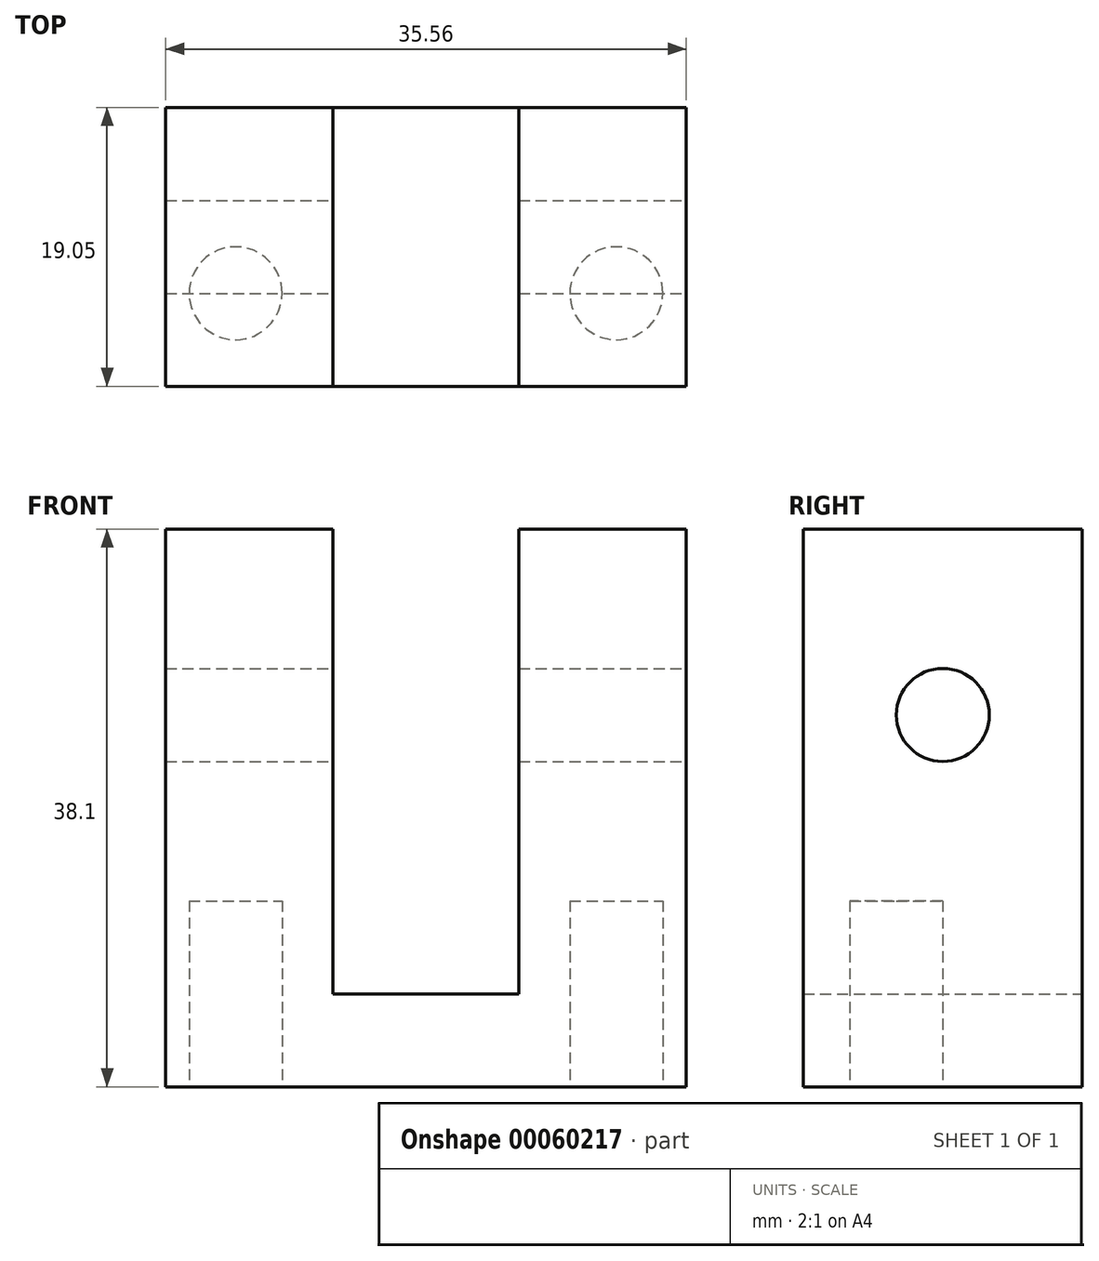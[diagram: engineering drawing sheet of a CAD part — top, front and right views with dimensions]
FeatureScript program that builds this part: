
annotation { "Feature Type Name" : "Feature", "Feature Type Description" : "" }
export const myFeature = defineFeature(function(context is Context, id is Id, definition is map)
    precondition{}
    {
        {
            var Q0;
            Q0=qCreatedBy(makeId("Front.planeOp"),FACE);
            var sketch = newSketch(context, id + "F0", { "sketchPlane" : qUnion([Q0])});
            skLineSegment(sketch, "E0", {"start": v(-17.78, 0) * mm, "end": v(-17.78, 38.1) * mm});
            skLineSegment(sketch, "E1", {"start": v(-17.78, 38.1) * mm, "end": v(-6.35, 38.1) * mm});
            skLineSegment(sketch, "E2", {"start": v(-6.35, 38.1) * mm, "end": v(-6.35, 6.35) * mm});
            skLineSegment(sketch, "E3", {"start": v(-6.35, 6.35) * mm, "end": v(6.35, 6.35) * mm});
            skLineSegment(sketch, "E4", {"start": v(6.35, 6.35) * mm, "end": v(6.35, 38.1) * mm});
            skLineSegment(sketch, "E5", {"start": v(6.35, 38.1) * mm, "end": v(17.78, 38.1) * mm});
            skLineSegment(sketch, "E6", {"start": v(17.78, 38.1) * mm, "end": v(17.78, 0) * mm});
            skLineSegment(sketch, "E7", {"start": v(17.78, 0) * mm, "end": v(-17.78, 0) * mm});
            skSolve(sketch);
        }
        {
            var Q0;
            Q0 = qSketchRegion(id + "F0", true);
            extrude(context, id + "F1", {"entities" : qUnion([Q0]), "depth" : 19.05 * mm});
        }
        {
            var Q0;
            Q0=makeQuery(id+"F1.opExtrude","SWEPT_FACE",FACE,{"disambiguationData":[OSD([sQuery(id+"F0.wireOp",EDGE,"E6")])]});
            var sketch = newSketch(context, id + "F2", { "sketchPlane" : qUnion([Q0])});
            skCircle(sketch, "E8", {"center": v(-9.53, 25.4) * mm, "radius": 3.18 * mm});
            skSolve(sketch);
        }
        {
            var Q0;
            Q0 = qSketchRegion(id + "F2", true);
            extrude(context, id + "F3", {"entities" : qUnion([Q0]), "operationType" : NewBodyOperationType.REMOVE, "oppositeDirection" : true, "depth" : 127 * mm});
        }
        {
            var Q0;
            Q0=makeQuery(id+"F1.opExtrude","SWEPT_FACE",FACE,{"disambiguationData":[OSD([sQuery(id+"F0.wireOp",EDGE,"E7")])]});
            var sketch = newSketch(context, id + "F4", { "sketchPlane" : qUnion([Q0])});
            skCircle(sketch, "E9", {"center": v(-13, 12.7) * mm, "radius": 3.18 * mm});
            skCircle(sketch, "E10", {"center": v(13, 12.7) * mm, "radius": 3.18 * mm});
            skSolve(sketch);
        }
        {
            var Q0;
            Q0 = qSketchRegion(id + "F4", true);
            extrude(context, id + "F5", {"entities" : qUnion([Q0]), "operationType" : NewBodyOperationType.REMOVE, "oppositeDirection" : true, "depth" : 12.7 * mm});
        }
    });
